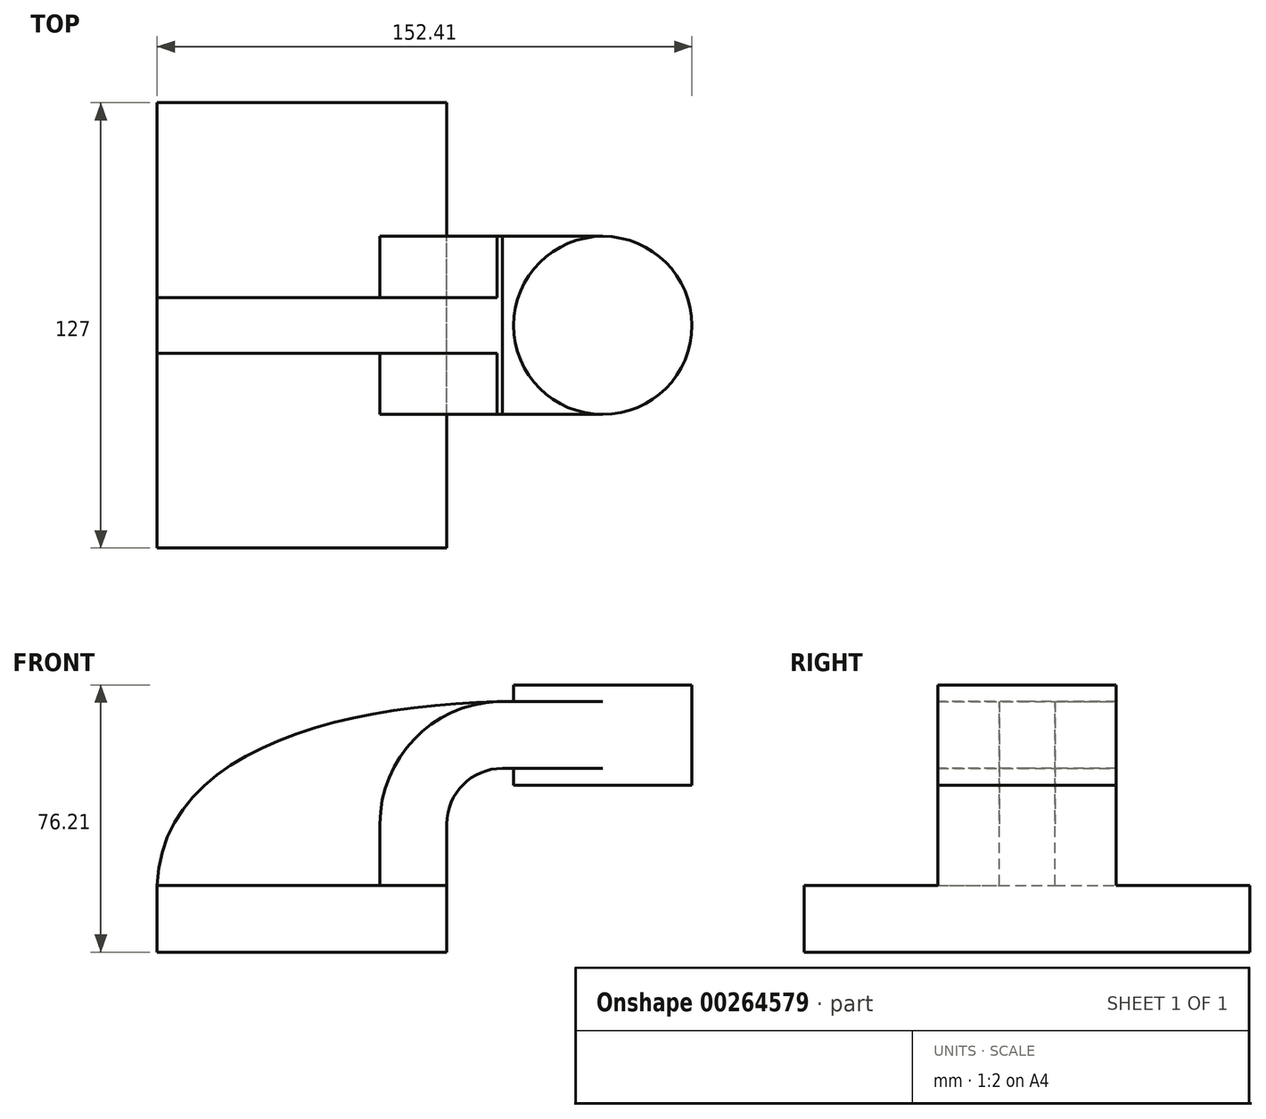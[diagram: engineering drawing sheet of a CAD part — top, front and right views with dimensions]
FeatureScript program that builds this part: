
annotation { "Feature Type Name" : "Feature", "Feature Type Description" : "" }
export const myFeature = defineFeature(function(context is Context, id is Id, definition is map)
    precondition{}
    {
        {
            var Q0;
            Q0=qCreatedBy(makeId("Front.planeOp"),FACE);
            var sketch = newSketch(context, id + "F0", { "sketchPlane" : qUnion([Q0])});
            skLineSegment(sketch, "E0.bottom", {"start": v(41.27, 9.53) * mm, "end": v(-41.28, 9.52) * mm});
            skLineSegment(sketch, "E0.top", {"start": v(41.28, -9.52) * mm, "end": v(-41.27, -9.53) * mm});
            skLineSegment(sketch, "E0.left", {"start": v(41.28, 9.53) * mm, "end": v(41.28, -9.52) * mm});
            skLineSegment(sketch, "E0.right", {"start": v(-41.28, 9.52) * mm, "end": v(-41.28, -9.53) * mm});
            skPoint(sketch, "E0.middle", {"position": v(0, 0) * mm});
            skLineSegment(sketch, "E1.bottom", {"start": v(60.32, 38.1) * mm, "end": v(111.12, 38.1) * mm});
            skLineSegment(sketch, "E1.top", {"start": v(60.32, 66.67) * mm, "end": v(111.12, 66.68) * mm});
            skLineSegment(sketch, "E1.left", {"start": v(60.32, 38.1) * mm, "end": v(60.32, 66.68) * mm});
            skLineSegment(sketch, "E1.right", {"start": v(111.12, 38.1) * mm, "end": v(111.12, 66.68) * mm});
            skPoint(sketch, "E1.middle", {"position": v(85.72, 52.39) * mm});
            skLineSegment(sketch, "E2", {"start": v(41.27, 9.53) * mm, "end": v(41.27, 27) * mm});
            skArc(sketch, "E3", {"start": v(41.27, 27) * mm, "mid": v(45.92, 38.23) * mm, "end": v(57.15, 42.88) * mm});
            skLineSegment(sketch, "E4", {"start": v(57.15, 42.88) * mm, "end": v(85.72, 42.88) * mm});
            skLineSegment(sketch, "E5.0", {"start": v(57.15, 61.93) * mm, "end": v(85.72, 61.93) * mm});
            skArc(sketch, "E5.1", {"start": v(22.22, 27) * mm, "mid": v(32.45, 51.7) * mm, "end": v(57.15, 61.93) * mm});
            skLineSegment(sketch, "E5.2", {"start": v(22.22, 9.53) * mm, "end": v(22.22, 27) * mm});
            skLineSegment(sketch, "E6", {"start": v(85.72, 38.1) * mm, "end": v(85.72, 66.67) * mm});
            skFitSpline(sketch, "E7", {"points": [v(-41.28, 9.53) * mm, v(57.15, 61.93) * mm], "startDerivative": vector(4.31, 116.55) * mm, "endDerivative": vector(135.8, 2.55) * mm});
            skSolve(sketch);
        }
        {
            var Q0;
            Q0=makeQuery(id+"F0.imprint","IMPRINT",FACE,{"disambiguationData":[TD([[makeQuery(id+"F0.imprint","IMPRINT",EDGE,{"derivedFrom":sQuery(id+"F0.wireOp",EDGE,"E0.top")}),-1.0]])]});
            extrude(context, id + "F1", {"entities" : qUnion([Q0]), "endBound" : BoundingType.SYMMETRIC, "depth" : 127 * mm});
        }
        {
            var Q0;
            {var subQ1=sQuery(id+"F0.wireOp",EDGE,"E2");Q0=makeQuery(id+"F0.imprint","IMPRINT",FACE,{"disambiguationData":[TD([[makeQuery(id+"F0.imprint","IMPRINT",EDGE,{"derivedFrom":subQ1}),1.0]])]});}
            var Q1;
            {var subQ0=sQuery(id+"F0.wireOp",EDGE,"E4");var subQ1=sQuery(id+"F0.wireOp",EDGE,"E1.left");var subQ2=makeQuery(id+"F0.imprint","INTERSECT",VERTEX,{"derivedFrom":[subQ1,subQ0]});Q1=makeQuery(id+"F0.imprint","IMPRINT",FACE,{"disambiguationData":[TD([[makeQuery(id+"F0.imprint","IMPRINT",EDGE,{"disambiguationData":[TD([[subQ2,-1.0]])],"derivedFrom":subQ1}),-1.0]])]});}
            extrude(context, id + "F2", {"entities" : qUnion([Q0, Q1]), "operationType" : NewBodyOperationType.ADD, "endBound" : BoundingType.SYMMETRIC, "depth" : 50.8 * mm});
        }
        {
            var Q0;
            {var subQ3=sQuery(id+"F0.wireOp",EDGE,"E5.2");Q0=makeQuery(id+"F0.imprint","IMPRINT",FACE,{"disambiguationData":[TD([[makeQuery(id+"F0.imprint","IMPRINT",EDGE,{"derivedFrom":subQ3}),1.0]])]});}
            extrude(context, id + "F3", {"entities" : qUnion([Q0]), "operationType" : NewBodyOperationType.ADD, "endBound" : BoundingType.SYMMETRIC, "depth" : 15.88 * mm});
        }
        {
            var Q0;
            {var subQ4=sQuery(id+"F0.wireOp",EDGE,"E1.right");Q0=makeQuery(id+"F0.imprint","IMPRINT",FACE,{"disambiguationData":[TD([[makeQuery(id+"F0.imprint","IMPRINT",EDGE,{"derivedFrom":subQ4}),1.0]])]});}
            var Q1;
            Q1=sQuery(id+"F0.wireOp",EDGE,"E6");
            revolve(context, id + "F4", {"operationType" : NewBodyOperationType.ADD, "entities" : qUnion([Q0]), "axis" : qUnion([Q1]), "revolveType" : RevolveType.FULL});
        }
    });
